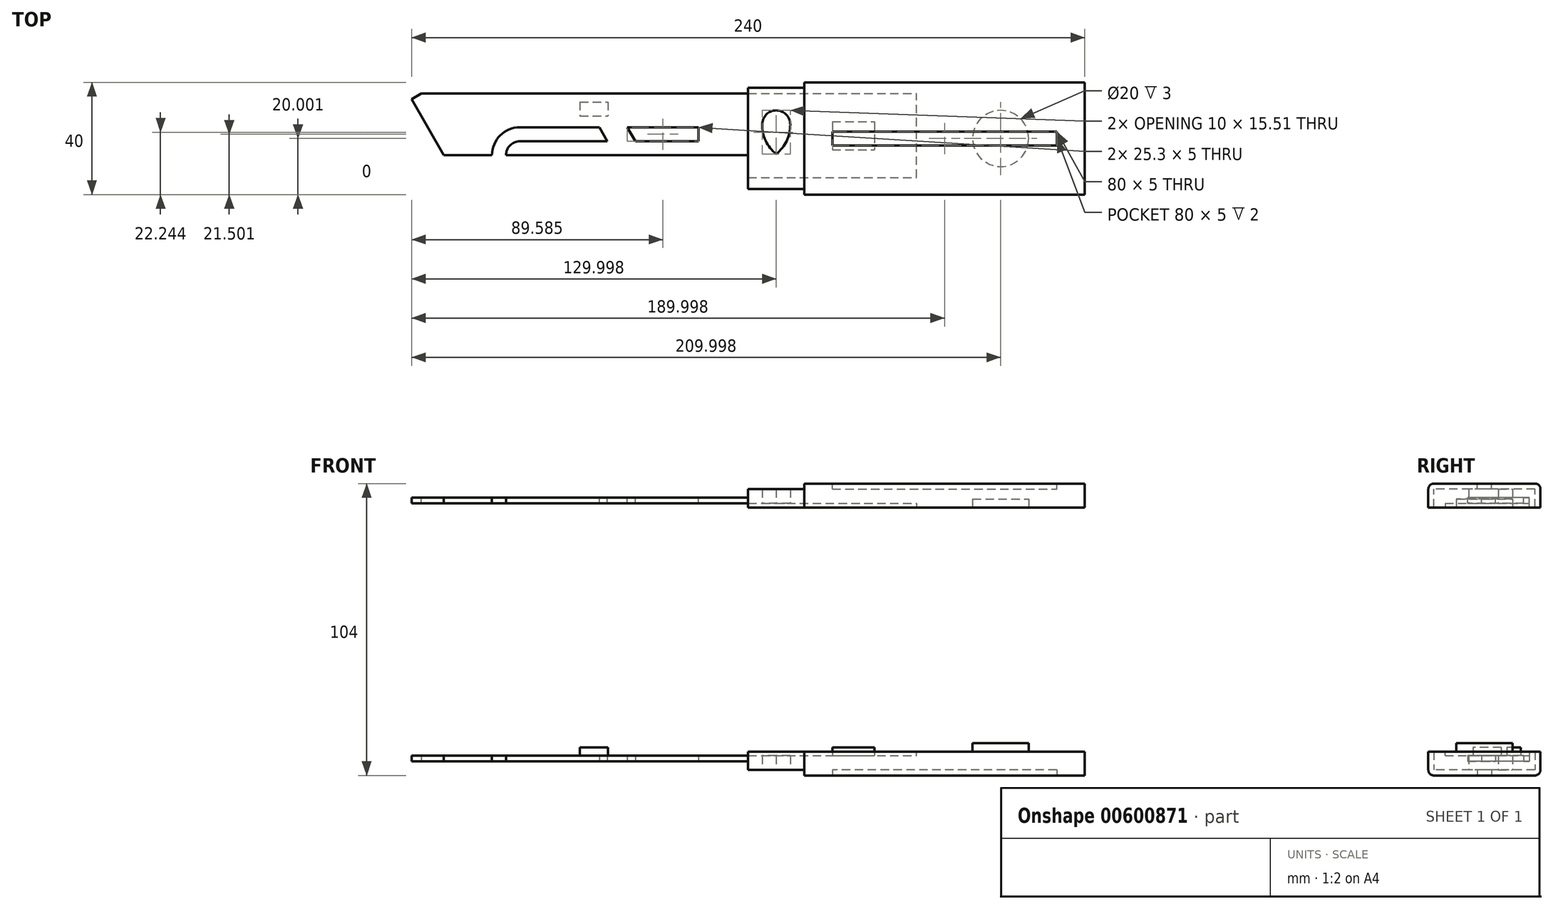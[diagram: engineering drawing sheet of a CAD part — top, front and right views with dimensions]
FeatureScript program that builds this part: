
annotation { "Feature Type Name" : "Feature", "Feature Type Description" : "" }
export const myFeature = defineFeature(function(context is Context, id is Id, definition is map)
    precondition{}
    {
        {
            var Q0;
            Q0=qCreatedBy(makeId("Top.planeOp"),FACE);
            var sketch = newSketch(context, id + "F0", { "sketchPlane" : qUnion([Q0])});
            skLineSegment(sketch, "E0.bottom", {"start": v(-23.26, 17.95) * mm, "end": v(-3.26, 17.95) * mm});
            skLineSegment(sketch, "E0.top", {"start": v(-23.26, -18.05) * mm, "end": v(-3.26, -18.05) * mm});
            skLineSegment(sketch, "E0.left", {"start": v(-23.26, 17.95) * mm, "end": v(-23.26, -18.05) * mm});
            skLineSegment(sketch, "E0.right", {"start": v(-3.26, 17.95) * mm, "end": v(-3.26, -18.05) * mm});
            skSolve(sketch);
        }
        {
            var Q0;
            Q0 = qSketchRegion(id + "F0", true);
            extrude(context, id + "F1", {"entities" : qUnion([Q0]), "depth" : 6.5 * mm, "offsetDistance" : 25 * mm});
        }
        {
            var Q0;
            Q0=makeQuery(id+"F1.opExtrude","SWEPT_FACE",FACE,{"disambiguationData":[OSD([sQuery(id+"F0.wireOp",EDGE,"E0.right")])]});
            var sketch = newSketch(context, id + "F2", { "sketchPlane" : qUnion([Q0])});
            skLineSegment(sketch, "E1.0", {"start": v(-14.05, 5) * mm, "end": v(15.95, 5) * mm});
            skLineSegment(sketch, "E1.1", {"start": v(-14.05, 5) * mm, "end": v(-14.05, 5) * mm});
            skLineSegment(sketch, "E1.2", {"start": v(15.95, 5) * mm, "end": v(-14.05, 5) * mm});
            skLineSegment(sketch, "E1.3", {"start": v(15.95, 5) * mm, "end": v(15.95, 5) * mm});
            skLineSegment(sketch, "E2.top", {"start": v(-14.05, 9.72) * mm, "end": v(15.95, 9.72) * mm});
            skLineSegment(sketch, "E2.left", {"start": v(-14.05, 5) * mm, "end": v(-14.05, 9.72) * mm});
            skLineSegment(sketch, "E2.right", {"start": v(15.95, 5) * mm, "end": v(15.95, 9.72) * mm});
            skSolve(sketch);
        }
        {
            var Q0;
            Q0=makeQuery(id+"F1.opExtrude","SWEPT_FACE",FACE,{"disambiguationData":[OSD([sQuery(id+"F0.wireOp",EDGE,"E0.left")])]});
            var sketch = newSketch(context, id + "F3", { "sketchPlane" : qUnion([Q0])});
            skLineSegment(sketch, "E3.bottom", {"start": v(-15.95, 6.5) * mm, "end": v(6.05, 6.5) * mm});
            skLineSegment(sketch, "E3.top", {"start": v(-15.95, 3) * mm, "end": v(6.05, 3) * mm});
            skLineSegment(sketch, "E3.left", {"start": v(-15.95, 6.5) * mm, "end": v(-15.95, 3) * mm});
            skLineSegment(sketch, "E3.right", {"start": v(6.05, 6.5) * mm, "end": v(6.05, 3) * mm});
            skSolve(sketch);
        }
        {
            var Q0;
            Q0=makeQuery(id+"F3.imprint","IMPRINT",FACE,{"disambiguationData":[TD([[makeQuery(id+"F3.imprint","IMPRINT",EDGE,{"derivedFrom":sQuery(id+"F3.wireOp",EDGE,"E3.bottom")}),-1.0]])]});
            extrude(context, id + "F4", {"entities" : qUnion([Q0]), "operationType" : NewBodyOperationType.ADD, "depth" : 120 * mm, "offsetDistance" : 25 * mm});
        }
        {
            var Q0;
            {var subQ0=sQuery(id+"F2.wireOp",EDGE,"E1.0");Q0=makeQuery(id+"F2.imprint","IMPRINT",FACE,{"disambiguationData":[TD([[makeQuery(id+"F2.imprint","IMPRINT",EDGE,{"derivedFrom":subQ0}),1.0]])]});}
            extrude(context, id + "F5", {"entities" : qUnion([Q0]), "operationType" : NewBodyOperationType.REMOVE, "endBound" : BoundingType.THROUGH_ALL, "oppositeDirection" : true, "depth" : 25 * mm, "offsetDistance" : 25 * mm});
        }
        {
            var Q0;
            Q0=makeQuery(id+"F4.opExtrude","SWEPT_FACE",FACE,{"disambiguationData":[OSD([sQuery(id+"F3.wireOp",EDGE,"E3.top")])]});
            var sketch = newSketch(context, id + "F6", { "sketchPlane" : qUnion([Q0])});
            skLineSegment(sketch, "E4", {"start": v(-143.26, -13.95) * mm, "end": v(-139.8, -15.95) * mm});
            skLineSegment(sketch, "E5", {"start": v(-143.26, -13.95) * mm, "end": v(-131.71, 6.05) * mm});
            skLineSegment(sketch, "E6.bottom", {"start": v(-76.32, -3.95) * mm, "end": v(-104.59, -3.95) * mm});
            skLineSegment(sketch, "E6.top", {"start": v(-73.44, 1.05) * mm, "end": v(-104.59, 1.05) * mm});
            skLineSegment(sketch, "E7", {"start": v(-73.44, 1.05) * mm, "end": v(-76.32, -3.95) * mm});
            skLineSegment(sketch, "E8.bottom", {"start": v(-66.32, 1.05) * mm, "end": v(-41.03, 1.05) * mm});
            skLineSegment(sketch, "E8.top", {"start": v(-66.32, -3.95) * mm, "end": v(-41.03, -3.95) * mm});
            skLineSegment(sketch, "E8.right", {"start": v(-41.03, 1.05) * mm, "end": v(-41.03, -3.95) * mm});
            skLineSegment(sketch, "E9", {"start": v(-66.32, -3.95) * mm, "end": v(-63.44, 1.05) * mm});
            skPoint(sketch, "E10.orphan", {"position": v(-73.44, -3.95) * mm});
            skArc(sketch, "E11", {"start": v(-104.59, -3.95) * mm, "mid": v(-111.66, -1.02) * mm, "end": v(-114.59, 6.05) * mm});
            skArc(sketch, "E12.0", {"start": v(-104.59, 1.05) * mm, "mid": v(-108.12, 2.51) * mm, "end": v(-109.59, 6.05) * mm});
            skSolve(sketch);
        }
        {
            var Q0;
            Q0 = qSketchRegion(id + "F6", true);
            var Q1;
            {var subQ0=sQuery(id+"F6.wireOp",EDGE,"E5");Q1=makeQuery(id+"F6.imprint","IMPRINT",FACE,{"disambiguationData":[TD([[makeQuery(id+"F6.imprint","IMPRINT",EDGE,{"derivedFrom":subQ0}),1.0]])]});}
            var Q2;
            {var subQ0=sQuery(id+"F6.wireOp",EDGE,"E4");Q2=makeQuery(id+"F6.imprint","IMPRINT",FACE,{"disambiguationData":[TD([[makeQuery(id+"F6.imprint","IMPRINT",EDGE,{"derivedFrom":subQ0}),-1.0]])]});}
            var Q3;
            Q3=makeQuery(id+"F6.imprint","IMPRINT",FACE,{"disambiguationData":[TD([[makeQuery(id+"F6.imprint","IMPRINT",EDGE,{"derivedFrom":sQuery(id+"F6.wireOp",EDGE,"E6.bottom")}),-1.0]])]});
            extrude(context, id + "F7", {"entities" : qUnion([Q0, Q1, Q2, Q3]), "operationType" : NewBodyOperationType.REMOVE, "oppositeDirection" : true, "depth" : 25 * mm, "offsetDistance" : 25 * mm});
        }
        {
            var Q0;
            Q0=makeQuery(id+"F1.opExtrude","SWEPT_FACE",FACE,{"disambiguationData":[OSD([sQuery(id+"F0.wireOp",EDGE,"E0.right")])]});
            var sketch = newSketch(context, id + "F8", { "sketchPlane" : qUnion([Q0])});
            skLineSegment(sketch, "E13.bottom", {"start": v(-20.05, 6.5) * mm, "end": v(19.95, 6.5) * mm});
            skLineSegment(sketch, "E13.top", {"start": v(-20.05, -2) * mm, "end": v(19.95, -2) * mm});
            skLineSegment(sketch, "E13.left", {"start": v(-20.05, 6.5) * mm, "end": v(-20.05, -2) * mm});
            skLineSegment(sketch, "E13.right", {"start": v(19.95, 6.5) * mm, "end": v(19.95, -2) * mm});
            skSolve(sketch);
        }
        {
            var Q0;
            Q0 = qSketchRegion(id + "F8", true);
            extrude(context, id + "F9", {"entities" : qUnion([Q0]), "operationType" : NewBodyOperationType.ADD, "depth" : 100 * mm, "offsetDistance" : 25 * mm});
        }
        {
            var Q0;
            {var subQ0=sQuery(id+"F8.wireOp",EDGE,"E13.bottom");Q0=makeQuery(id+"F9.boolean.opBoolean","SPLIT",FACE,{"disambiguationData":[TD([makeQuery(id+"F5.boolean.opBoolean","COPY",FACE,{"derivedFrom":makeQuery(id+"F5.opExtrude","SWEPT_FACE",FACE,{"disambiguationData":[OSD([sQuery(id+"F2.wireOp",EDGE,"E1.0")])]})})])],"derivedFrom":makeQuery(id+"F9.opExtrude","CAP_FACE",FACE,{"disambiguationData":[OSD([subQ0,sQuery(id+"F8.wireOp",EDGE,"E13.top"),sQuery(id+"F8.wireOp",EDGE,"E13.left"),sQuery(id+"F8.wireOp",EDGE,"E13.right")])],"isStart":true})});}
            extrude(context, id + "F10", {"entities" : qUnion([Q0]), "operationType" : NewBodyOperationType.REMOVE, "oppositeDirection" : true, "depth" : 40 * mm, "offsetDistance" : 25 * mm});
        }
        {
            var Q0;
            Q0=qCreatedBy(makeId("Top.planeOp"),FACE);
            cPlane(context, id + "F11", {"entities" : qUnion([Q0]), "cplaneType" : CPlaneType.OFFSET, "offset" : 50 * mm, "width" : 150 * mm, "height" : 150 * mm});
        }
        {
            var Q0;
            Q0=makeQuery(id+"F1.opExtrude","SWEPT_BODY",BODY,{"disambiguationData":[OSD([sQuery(id+"F0.wireOp",EDGE,"E0.bottom"),sQuery(id+"F0.wireOp",EDGE,"E0.top"),sQuery(id+"F0.wireOp",EDGE,"E0.left"),sQuery(id+"F0.wireOp",EDGE,"E0.right")])]});
            var Q1;
            Q1=qCreatedBy(id+"F11.planeOp",FACE);
            mirror(context, id + "F12", {"entities" : qUnion([Q0]), "mirrorPlane" : qUnion([Q1])});
        }
        {
            var Q0;
            {var subQ0=sQuery(id+"F2.wireOp",EDGE,"E1.0");Q0=makeQuery(id+"F10.boolean.opBoolean","MERGE",FACE,{"derivedFrom":[makeQuery(id+"F5.boolean.opBoolean","COPY",FACE,{"derivedFrom":makeQuery(id+"F5.opExtrude","SWEPT_FACE",FACE,{"disambiguationData":[OSD([subQ0])]})}),makeQuery(id+"F10.opExtrude","SWEPT_FACE",FACE,{"disambiguationData":[OSD([subQ0])]})]});}
            var sketch = newSketch(context, id + "F13", { "sketchPlane" : qUnion([Q0])});
            skLineSegment(sketch, "E14.bottom", {"start": v(-83.26, 12.95) * mm, "end": v(-73.26, 12.95) * mm});
            skLineSegment(sketch, "E14.top", {"start": v(-83.26, 7.95) * mm, "end": v(-73.26, 7.95) * mm});
            skLineSegment(sketch, "E14.left", {"start": v(-83.26, 12.95) * mm, "end": v(-83.26, 7.95) * mm});
            skLineSegment(sketch, "E14.right", {"start": v(-73.26, 12.95) * mm, "end": v(-73.26, 7.95) * mm});
            skLineSegment(sketch, "E15.bottom", {"start": v(6.74, 5.95) * mm, "end": v(21.74, 5.95) * mm});
            skLineSegment(sketch, "E15.top", {"start": v(6.74, -4.05) * mm, "end": v(21.74, -4.05) * mm});
            skLineSegment(sketch, "E15.left", {"start": v(6.74, 5.95) * mm, "end": v(6.74, -4.05) * mm});
            skLineSegment(sketch, "E15.right", {"start": v(21.74, 5.95) * mm, "end": v(21.74, -4.05) * mm});
            skSolve(sketch);
        }
        {
            var Q0;
            Q0=makeQuery(id+"F13.imprint","IMPRINT",FACE,{"disambiguationData":[TD([[makeQuery(id+"F13.imprint","IMPRINT",EDGE,{"derivedFrom":sQuery(id+"F13.wireOp",EDGE,"E14.bottom")}),-1.0]])]});
            var Q1;
            Q1=makeQuery(id+"F13.imprint","IMPRINT",FACE,{"disambiguationData":[TD([[makeQuery(id+"F13.imprint","IMPRINT",EDGE,{"derivedFrom":sQuery(id+"F13.wireOp",EDGE,"E15.bottom")}),-1.0]])]});
            extrude(context, id + "F14", {"entities" : qUnion([Q0, Q1]), "operationType" : NewBodyOperationType.ADD, "depth" : 3 * mm, "offsetDistance" : 25 * mm});
        }
        {
            var Q0;
            Q0=makeQuery(id+"F0.imprint","IMPRINT",FACE,{"disambiguationData":[TD([[makeQuery(id+"F0.imprint","IMPRINT",EDGE,{"derivedFrom":sQuery(id+"F0.wireOp",EDGE,"E0.bottom")}),-1.0]])]});
            var sketch = newSketch(context, id + "F15", { "sketchPlane" : qUnion([Q0])});
            skCircle(sketch, "E16", {"center": v(-13.26, 4.95) * mm, "radius": 5 * mm});
            skArc(sketch, "E17", {"start": v(-13.26, -5.56) * mm, "mid": v(-9.52, -0.9) * mm, "end": v(-8.26, 4.95) * mm});
            skArc(sketch, "E18", {"start": v(-18.26, 4.95) * mm, "mid": v(-17, -0.9) * mm, "end": v(-13.26, -5.56) * mm});
            skSolve(sketch);
        }
        {
            var Q0;
            {var subQ0=sQuery(id+"F15.wireOp",EDGE,"E16");var subQ1=makeQuery(id+"F15.imprint","INTERSECT",VERTEX,{"derivedFrom":[subQ0,sQuery(id+"F15.wireOp",EDGE,"E17")]});Q0=makeQuery(id+"F15.imprint","IMPRINT",FACE,{"disambiguationData":[TD([[makeQuery(id+"F15.imprint","IMPRINT",EDGE,{"disambiguationData":[TD([[subQ1,-1.0]])],"derivedFrom":subQ0}),1.0]])]});}
            var Q1;
            {var subQ0=sQuery(id+"F15.wireOp",EDGE,"E17");Q1=makeQuery(id+"F15.imprint","IMPRINT",FACE,{"disambiguationData":[TD([[makeQuery(id+"F15.imprint","IMPRINT",EDGE,{"derivedFrom":subQ0}),1.0]])]});}
            extrude(context, id + "F16", {"entities" : qUnion([Q0, Q1]), "operationType" : NewBodyOperationType.REMOVE, "endBound" : BoundingType.THROUGH_ALL, "depth" : 100 * mm, "offsetDistance" : 25 * mm});
        }
        {
            var Q0;
            Q0=makeQuery(id+"F9.opExtrude","SWEPT_FACE",FACE,{"disambiguationData":[OSD([sQuery(id+"F8.wireOp",EDGE,"E13.top")])]});
            var sketch = newSketch(context, id + "F17", { "sketchPlane" : qUnion([Q0])});
            skLineSegment(sketch, "E19.bottom", {"start": v(86.74, -2.45) * mm, "end": v(6.74, -2.45) * mm});
            skLineSegment(sketch, "E19.top", {"start": v(86.74, 2.55) * mm, "end": v(6.74, 2.55) * mm});
            skLineSegment(sketch, "E19.left", {"start": v(86.74, -2.45) * mm, "end": v(86.74, 2.55) * mm});
            skLineSegment(sketch, "E19.right", {"start": v(6.74, -2.45) * mm, "end": v(6.74, 2.55) * mm});
            skSolve(sketch);
        }
        {
            var Q0;
            Q0=makeQuery(id+"F17.imprint","IMPRINT",FACE,{"disambiguationData":[TD([[makeQuery(id+"F17.imprint","IMPRINT",EDGE,{"derivedFrom":sQuery(id+"F17.wireOp",EDGE,"E19.bottom")}),-1.0]])]});
            extrude(context, id + "F18", {"entities" : qUnion([Q0]), "operationType" : NewBodyOperationType.REMOVE, "oppositeDirection" : true, "depth" : 2 * mm, "offsetDistance" : 25 * mm});
        }
        {
            var Q0;
            Q0=makeQuery(id+"F18.boolean.opBoolean","COPY",FACE,{"derivedFrom":makeQuery(id+"F18.opExtrude","SWEPT_FACE",FACE,{"disambiguationData":[OSD([sQuery(id+"F17.wireOp",EDGE,"E19.right")])]})});
            var sketch = newSketch(context, id + "F19", { "sketchPlane" : qUnion([Q0])});
            skArc(sketch, "E20", {"start": v(2.45, -2) * mm, "mid": v(-0.05, 0) * mm, "end": v(-2.55, -2) * mm});
            skSolve(sketch);
        }
        {
            var Q0;
            Q0=makeQuery(id+"F19.imprint","IMPRINT",FACE,{"disambiguationData":[TD([[makeQuery(id+"F19.imprint","IMPRINT",EDGE,{"derivedFrom":sQuery(id+"F19.wireOp",EDGE,"E20")}),1.0]])]});
            var Q1;
            Q1=sQuery(id+"F19.wireOp",EDGE,"E20");
            extrude(context, id + "F20", {"entities" : qUnion([Q0]), "bodyType" : ToolBodyType.SURFACE, "surfaceEntities" : qUnion([Q1]), "endBound" : BoundingType.UP_TO_NEXT, "depth" : 25 * mm, "offsetDistance" : 25 * mm});
        }
        {
            var Q0;
            Q0=makeQuery(id+"F12.opPattern","COPY",FACE,{"derivedFrom":makeQuery(id+"F9.opExtrude","SWEPT_FACE",FACE,{"disambiguationData":[OSD([sQuery(id+"F8.wireOp",EDGE,"E13.top")])]}),"instanceName":"1"});
            var sketch = newSketch(context, id + "F21", { "sketchPlane" : qUnion([Q0])});
            skLineSegment(sketch, "E21.bottom", {"start": v(6.74, 2.45) * mm, "end": v(86.74, 2.45) * mm});
            skLineSegment(sketch, "E21.top", {"start": v(6.74, -2.55) * mm, "end": v(86.74, -2.55) * mm});
            skLineSegment(sketch, "E21.left", {"start": v(6.74, 2.45) * mm, "end": v(6.74, -2.55) * mm});
            skLineSegment(sketch, "E21.right", {"start": v(86.74, 2.45) * mm, "end": v(86.74, -2.55) * mm});
            skSolve(sketch);
        }
        {
            var Q0;
            Q0=makeQuery(id+"F21.imprint","IMPRINT",FACE,{"disambiguationData":[TD([[makeQuery(id+"F21.imprint","IMPRINT",EDGE,{"derivedFrom":sQuery(id+"F21.wireOp",EDGE,"E21.bottom")}),-1.0]])]});
            extrude(context, id + "F22", {"entities" : qUnion([Q0]), "operationType" : NewBodyOperationType.REMOVE, "oppositeDirection" : true, "depth" : 2 * mm, "offsetDistance" : 25 * mm});
        }
        {
            var Q0;
            Q0=makeQuery(id+"F22.boolean.opBoolean","COPY",FACE,{"derivedFrom":makeQuery(id+"F22.opExtrude","SWEPT_FACE",FACE,{"disambiguationData":[OSD([sQuery(id+"F21.wireOp",EDGE,"E21.left")])]})});
            var sketch = newSketch(context, id + "F23", { "sketchPlane" : qUnion([Q0])});
            skArc(sketch, "E22", {"start": v(-2.55, 102) * mm, "mid": v(-0.05, 100) * mm, "end": v(2.45, 102) * mm});
            skSolve(sketch);
        }
        {
            var Q0;
            {var subQ1=sQuery(id+"F21.wireOp",EDGE,"E21.left");var subQ2=makeQuery(id+"F22.boolean.opBoolean","COPY",EDGE,{"derivedFrom":makeQuery(id+"F22.opExtrude","CAP_EDGE",EDGE,{"disambiguationData":[OSD([subQ1])],"isStart":true})});Q0=makeQuery(id+"F23.imprint","IMPRINT",FACE,{"disambiguationData":[TD([[makeQuery(id+"F23.imprint","IMPRINT",EDGE,{"derivedFrom":subQ2}),1.0]])]});}
            var Q1;
            Q1=sQuery(id+"F23.wireOp",EDGE,"E22");
            extrude(context, id + "F24", {"entities" : qUnion([Q0]), "bodyType" : ToolBodyType.SURFACE, "surfaceEntities" : qUnion([Q1]), "endBound" : BoundingType.UP_TO_NEXT, "depth" : 25 * mm, "offsetDistance" : 25 * mm});
        }
        {
            var Q0;
            Q0=makeQuery(id+"F9.opExtrude","SWEPT_EDGE",EDGE,{"disambiguationData":[OSD([sQuery(id+"F8.wireOp",EDGE,"E13.top"),sQuery(id+"F8.wireOp",EDGE,"E13.right")])]});
            var Q1;
            Q1=makeQuery(id+"F9.opExtrude","SWEPT_EDGE",EDGE,{"disambiguationData":[OSD([sQuery(id+"F8.wireOp",EDGE,"E13.top"),sQuery(id+"F8.wireOp",EDGE,"E13.left")])]});
            var Q2;
            Q2=makeQuery(id+"F12.opPattern","COPY",EDGE,{"derivedFrom":makeQuery(id+"F9.opExtrude","SWEPT_EDGE",EDGE,{"disambiguationData":[OSD([sQuery(id+"F8.wireOp",EDGE,"E13.top"),sQuery(id+"F8.wireOp",EDGE,"E13.left")])]}),"instanceName":"1"});
            var Q3;
            Q3=makeQuery(id+"F12.opPattern","COPY",EDGE,{"derivedFrom":makeQuery(id+"F9.opExtrude","SWEPT_EDGE",EDGE,{"disambiguationData":[OSD([sQuery(id+"F8.wireOp",EDGE,"E13.top"),sQuery(id+"F8.wireOp",EDGE,"E13.right")])]}),"instanceName":"1"});
            fillet(context, id + "F25", {"entities" : qUnion([Q0, Q1, Q2, Q3]), "radius" : 2 * mm, "tangentPropagation" : true, "allowEdgeOverflow" : false});
        }
        {
            var Q0;
            {var subQ0=sQuery(id+"F0.wireOp",EDGE,"E0.top");var subQ1=sQuery(id+"F0.wireOp",EDGE,"E0.left");var subQ3=sQuery(id+"F0.wireOp",EDGE,"E0.right");var subQ5=sQuery(id+"F0.wireOp",EDGE,"E0.bottom");var subQ6=makeQuery(id+"F4.boolean.opBoolean","MERGE",FACE,{"derivedFrom":[makeQuery(id+"F1.opExtrude","CAP_FACE",FACE,{"disambiguationData":[OSD([subQ5,subQ0,subQ1,subQ3])],"isStart":false}),makeQuery(id+"F4.opExtrude","SWEPT_FACE",FACE,{"disambiguationData":[OSD([sQuery(id+"F3.wireOp",EDGE,"E3.bottom")])]})]});Q0=makeQuery(id+"F9.boolean.opBoolean","MERGE",FACE,{"derivedFrom":[makeQuery(id+"F5.boolean.opBoolean","SPLIT",FACE,{"disambiguationData":[TD([makeQuery(id+"F1.opExtrude","SWEPT_FACE",FACE,{"disambiguationData":[OSD([subQ5])]})])],"derivedFrom":subQ6}),makeQuery(id+"F5.boolean.opBoolean","SPLIT",FACE,{"disambiguationData":[TD([makeQuery(id+"F1.opExtrude","SWEPT_FACE",FACE,{"disambiguationData":[OSD([subQ0])]})])],"derivedFrom":subQ6}),makeQuery(id+"F9.opExtrude","SWEPT_FACE",FACE,{"disambiguationData":[OSD([sQuery(id+"F8.wireOp",EDGE,"E13.bottom")])]})]});}
            var sketch = newSketch(context, id + "F26", { "sketchPlane" : qUnion([Q0])});
            skCircle(sketch, "E23", {"center": v(66.74, -0.05) * mm, "radius": 10 * mm});
            skSolve(sketch);
        }
        {
            var Q0;
            {var subQ0=sQuery(id+"F0.wireOp",EDGE,"E0.top");var subQ1=sQuery(id+"F0.wireOp",EDGE,"E0.left");var subQ3=sQuery(id+"F0.wireOp",EDGE,"E0.right");var subQ5=sQuery(id+"F0.wireOp",EDGE,"E0.bottom");var subQ6=makeQuery(id+"F4.boolean.opBoolean","MERGE",FACE,{"derivedFrom":[makeQuery(id+"F1.opExtrude","CAP_FACE",FACE,{"disambiguationData":[OSD([subQ5,subQ0,subQ1,subQ3])],"isStart":false}),makeQuery(id+"F4.opExtrude","SWEPT_FACE",FACE,{"disambiguationData":[OSD([sQuery(id+"F3.wireOp",EDGE,"E3.bottom")])]})]});Q0=makeQuery(id+"F12.opPattern","COPY",FACE,{"derivedFrom":makeQuery(id+"F9.boolean.opBoolean","MERGE",FACE,{"derivedFrom":[makeQuery(id+"F5.boolean.opBoolean","SPLIT",FACE,{"disambiguationData":[TD([makeQuery(id+"F1.opExtrude","SWEPT_FACE",FACE,{"disambiguationData":[OSD([subQ5])]})])],"derivedFrom":subQ6}),makeQuery(id+"F5.boolean.opBoolean","SPLIT",FACE,{"disambiguationData":[TD([makeQuery(id+"F1.opExtrude","SWEPT_FACE",FACE,{"disambiguationData":[OSD([subQ0])]})])],"derivedFrom":subQ6}),makeQuery(id+"F9.opExtrude","SWEPT_FACE",FACE,{"disambiguationData":[OSD([sQuery(id+"F8.wireOp",EDGE,"E13.bottom")])]})]}),"instanceName":"1"});}
            var sketch = newSketch(context, id + "F27", { "sketchPlane" : qUnion([Q0])});
            skCircle(sketch, "E24", {"center": v(66.74, 0.05) * mm, "radius": 10 * mm});
            skSolve(sketch);
        }
        {
            var Q0;
            Q0=makeQuery(id+"F27.imprint","IMPRINT",FACE,{"disambiguationData":[TD([[makeQuery(id+"F27.imprint","IMPRINT",EDGE,{"derivedFrom":sQuery(id+"F27.wireOp",EDGE,"E24")}),1.0]])]});
            extrude(context, id + "F28", {"entities" : qUnion([Q0]), "operationType" : NewBodyOperationType.REMOVE, "oppositeDirection" : true, "depth" : 3 * mm, "offsetDistance" : 25 * mm});
        }
        {
            var Q0;
            Q0=makeQuery(id+"F26.imprint","IMPRINT",FACE,{"disambiguationData":[TD([[makeQuery(id+"F26.imprint","IMPRINT",EDGE,{"derivedFrom":sQuery(id+"F26.wireOp",EDGE,"E23")}),1.0]])]});
            extrude(context, id + "F29", {"entities" : qUnion([Q0]), "operationType" : NewBodyOperationType.ADD, "depth" : 3 * mm, "offsetDistance" : 25 * mm});
        }
    });
